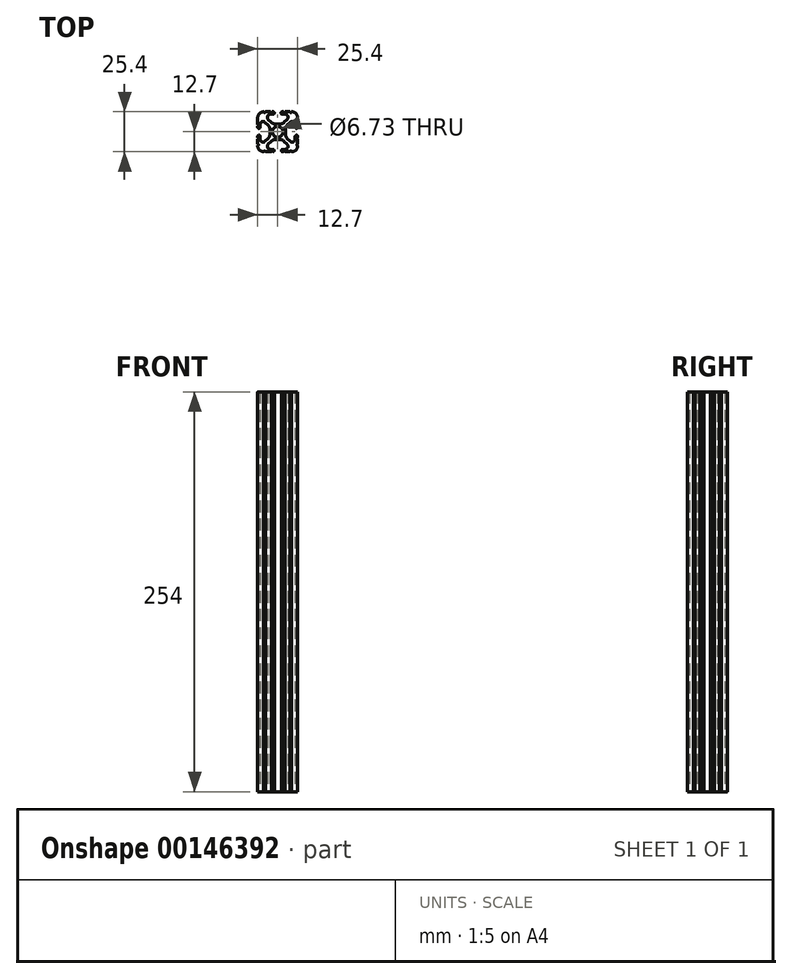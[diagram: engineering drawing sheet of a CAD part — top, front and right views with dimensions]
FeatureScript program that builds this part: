
annotation { "Feature Type Name" : "Feature", "Feature Type Description" : "" }
export const myFeature = defineFeature(function(context is Context, id is Id, definition is map)
    precondition{}
    {
        {
            var Q0;
            Q0=qCreatedBy(makeId("Top.planeOp"),FACE);
            var sketch = newSketch(context, id + "F0", { "sketchPlane" : qUnion([Q0])});
            skCircle(sketch, "E0", {"center": v(-12.7, 12.7) * mm, "radius": 3.36 * mm});
            skLineSegment(sketch, "E1.bottom", {"start": v(-11.24, 17.64) * mm, "end": v(-14.16, 17.64) * mm});
            skLineSegment(sketch, "E1.top", {"start": v(-11.24, 7.76) * mm, "end": v(-14.16, 7.76) * mm});
            skLineSegment(sketch, "E1.left", {"start": v(-7.76, 14.16) * mm, "end": v(-7.76, 11.24) * mm});
            skLineSegment(sketch, "E1.right", {"start": v(-17.64, 14.16) * mm, "end": v(-17.64, 11.24) * mm});
            skPoint(sketch, "E2.visualSharp", {"position": v(-25.4, 25.4) * mm});
            skPoint(sketch, "E3.visualSharp", {"position": v(0, 25.4) * mm});
            skPoint(sketch, "E4.visualSharp", {"position": v(0, 0) * mm});
            skPoint(sketch, "E5.visualSharp", {"position": v(-25.4, 0) * mm});
            skLineSegment(sketch, "E6.0", {"start": v(-18.7, 20.6) * mm, "end": v(-16.85, 18.76) * mm});
            skLineSegment(sketch, "E7.0", {"start": v(-20.6, 18.7) * mm, "end": v(-18.76, 16.85) * mm});
            skPoint(sketch, "E8.orphan", {"position": v(-23.85, 1.55) * mm});
            skPoint(sketch, "E9.orphan", {"position": v(-23.85, 23.85) * mm});
            skPoint(sketch, "E10.orphan", {"position": v(-1.55, 23.85) * mm});
            skPoint(sketch, "E11.orphan", {"position": v(-1.55, 1.55) * mm});
            skLineSegment(sketch, "E12", {"start": v(-8.55, 6.64) * mm, "end": v(-6.7, 4.8) * mm});
            skLineSegment(sketch, "E13.0", {"start": v(-18.7, 4.8) * mm, "end": v(-16.85, 6.64) * mm});
            skLineSegment(sketch, "E14.0", {"start": v(-20.6, 6.7) * mm, "end": v(-18.76, 8.55) * mm});
            skLineSegment(sketch, "E15.0", {"start": v(-8.55, 18.76) * mm, "end": v(-6.7, 20.6) * mm});
            skPoint(sketch, "E16.visualSharp", {"position": v(-23.85, 21.95) * mm});
            skArc(sketch, "E16.filletArc", {"start": v(-20.6, 18.7) * mm, "mid": v(-22.68, 19.1) * mm, "end": v(-23.85, 17.35) * mm});
            skPoint(sketch, "E17.visualSharp", {"position": v(-21.95, 23.85) * mm});
            skArc(sketch, "E17.filletArc", {"start": v(-17.35, 23.85) * mm, "mid": v(-19.1, 22.68) * mm, "end": v(-18.7, 20.6) * mm});
            skPoint(sketch, "E18.visualSharp", {"position": v(-5.34, 23.85) * mm});
            skLineSegment(sketch, "E19", {"start": v(-17.35, 23.85) * mm, "end": v(-15.58, 23.85) * mm});
            skLineSegment(sketch, "E20", {"start": v(-23.85, 17.35) * mm, "end": v(-23.85, 15.62) * mm});
            skLineSegment(sketch, "E21", {"start": v(-8.05, 1.55) * mm, "end": v(-9.78, 1.55) * mm});
            skArc(sketch, "E22.filletArc", {"start": v(-6.7, 20.6) * mm, "mid": v(-6.3, 22.68) * mm, "end": v(-8.05, 23.85) * mm});
            skPoint(sketch, "E23.visualSharp", {"position": v(-1.55, 3.45) * mm});
            skPoint(sketch, "E24.visualSharp", {"position": v(-3.45, 1.55) * mm});
            skArc(sketch, "E24.filletArc", {"start": v(-8.05, 1.55) * mm, "mid": v(-6.3, 2.73) * mm, "end": v(-6.7, 4.8) * mm});
            skArc(sketch, "E25.filletArc", {"start": v(-18.7, 4.8) * mm, "mid": v(-19.1, 2.73) * mm, "end": v(-17.35, 1.55) * mm});
            skArc(sketch, "E26.filletArc", {"start": v(-23.85, 8.05) * mm, "mid": v(-22.68, 6.3) * mm, "end": v(-20.6, 6.7) * mm});
            skLineSegment(sketch, "E27.bottom", {"start": v(-4.9, 0) * mm, "end": v(-8.05, 0) * mm});
            skLineSegment(sketch, "E27.top", {"start": v(-4.92, 25.4) * mm, "end": v(-8.05, 25.4) * mm});
            skLineSegment(sketch, "E27.left", {"start": v(0, 4.9) * mm, "end": v(0, 8.05) * mm});
            skLineSegment(sketch, "E27.right", {"start": v(-25.4, 4.9) * mm, "end": v(-25.4, 8.05) * mm});
            skArc(sketch, "E28.filletArc", {"start": v(-25.4, 3.81) * mm, "mid": v(-24.28, 1.12) * mm, "end": v(-21.59, 0) * mm});
            skArc(sketch, "E29.filletArc", {"start": v(-3.81, 0) * mm, "mid": v(-1.12, 1.12) * mm, "end": v(0, 3.8) * mm});
            skArc(sketch, "E30.filletArc", {"start": v(0, 21.59) * mm, "mid": v(-1.12, 24.28) * mm, "end": v(-3.8, 25.4) * mm});
            skArc(sketch, "E31.filletArc", {"start": v(-21.59, 25.4) * mm, "mid": v(-24.28, 24.28) * mm, "end": v(-25.4, 21.59) * mm});
            skPoint(sketch, "E32.newPointA", {"position": v(-17.64, 7.76) * mm});
            skArc(sketch, "E32.filletArc", {"start": v(-14.16, 7.76) * mm, "mid": v(-15.62, 7.47) * mm, "end": v(-16.85, 6.64) * mm});
            skPoint(sketch, "E33.newPointA", {"position": v(-7.76, 7.76) * mm});
            skArc(sketch, "E33.filletArc", {"start": v(-8.55, 6.64) * mm, "mid": v(-9.78, 7.47) * mm, "end": v(-11.24, 7.76) * mm});
            skArc(sketch, "E34.filletArc", {"start": v(-7.76, 11.24) * mm, "mid": v(-7.47, 9.78) * mm, "end": v(-6.64, 8.55) * mm});
            skArc(sketch, "E35.filletArc", {"start": v(-6.64, 16.85) * mm, "mid": v(-7.47, 15.62) * mm, "end": v(-7.76, 14.16) * mm});
            skPoint(sketch, "E36.newPointB", {"position": v(-7.76, 17.64) * mm});
            skArc(sketch, "E36.filletArc", {"start": v(-11.24, 17.64) * mm, "mid": v(-9.78, 17.93) * mm, "end": v(-8.55, 18.76) * mm});
            skPoint(sketch, "E37.newPointB", {"position": v(-17.64, 17.64) * mm});
            skArc(sketch, "E37.filletArc", {"start": v(-16.85, 18.76) * mm, "mid": v(-15.62, 17.93) * mm, "end": v(-14.16, 17.64) * mm});
            skArc(sketch, "E38.filletArc", {"start": v(-17.64, 14.16) * mm, "mid": v(-17.93, 15.62) * mm, "end": v(-18.76, 16.85) * mm});
            skArc(sketch, "E39.filletArc", {"start": v(-18.76, 8.55) * mm, "mid": v(-17.93, 9.78) * mm, "end": v(-17.64, 11.24) * mm});
            skLineSegment(sketch, "E40", {"start": v(-6.64, 8.55) * mm, "end": v(-4.8, 6.7) * mm});
            skPoint(sketch, "E41.visualSharp", {"position": v(-1.55, 21.95) * mm});
            skArc(sketch, "E42.filletArc", {"start": v(-4.8, 6.7) * mm, "mid": v(-2.73, 6.3) * mm, "end": v(-1.55, 8.05) * mm});
            skLineSegment(sketch, "E43", {"start": v(-1.55, 8.05) * mm, "end": v(-1.55, 9.78) * mm});
            skLineSegment(sketch, "E44", {"start": v(-6.64, 16.85) * mm, "end": v(-4.8, 18.7) * mm});
            skArc(sketch, "E45.filletArc", {"start": v(-1.55, 17.35) * mm, "mid": v(-2.73, 19.1) * mm, "end": v(-4.8, 18.7) * mm});
            skArc(sketch, "E46", {"start": v(-23.85, 9.78) * mm, "mid": v(-24.63, 10.56) * mm, "end": v(-25.4, 9.78) * mm});
            skArc(sketch, "E47", {"start": v(-25.4, 15.62) * mm, "mid": v(-24.63, 14.86) * mm, "end": v(-23.85, 15.62) * mm});
            skArc(sketch, "E48", {"start": v(-15.62, 23.85) * mm, "mid": v(-14.83, 24.63) * mm, "end": v(-15.62, 25.4) * mm});
            skArc(sketch, "E49", {"start": v(-9.78, 25.4) * mm, "mid": v(-10.6, 24.63) * mm, "end": v(-9.78, 23.85) * mm});
            skArc(sketch, "E50", {"start": v(-1.55, 15.62) * mm, "mid": v(-0.77, 14.88) * mm, "end": v(0, 15.62) * mm});
            skArc(sketch, "E51", {"start": v(0, 9.78) * mm, "mid": v(-0.77, 10.5) * mm, "end": v(-1.55, 9.78) * mm});
            skArc(sketch, "E52", {"start": v(-9.78, 1.55) * mm, "mid": v(-10.4, 0.77) * mm, "end": v(-9.78, 0) * mm});
            skArc(sketch, "E53", {"start": v(-15.62, 0) * mm, "mid": v(-14.85, 0.77) * mm, "end": v(-15.62, 1.55) * mm});
            skLineSegment(sketch, "E54.trimOffspring", {"start": v(-15.62, 1.55) * mm, "end": v(-17.35, 1.55) * mm});
            skLineSegment(sketch, "E55.trimOffspring", {"start": v(-16.7, 0) * mm, "end": v(-20.5, 0) * mm});
            skLineSegment(sketch, "E56.trimOffspring", {"start": v(-1.55, 15.62) * mm, "end": v(-1.55, 17.35) * mm});
            skLineSegment(sketch, "E57.trimOffspring", {"start": v(0, 15.62) * mm, "end": v(0, 16.26) * mm});
            skLineSegment(sketch, "E58.trimOffspring", {"start": v(-23.85, 9.78) * mm, "end": v(-23.85, 8.05) * mm});
            skLineSegment(sketch, "E59.trimOffspring", {"start": v(-25.4, 15.62) * mm, "end": v(-25.4, 16.26) * mm});
            skLineSegment(sketch, "E60.trimOffspring", {"start": v(-9.86, 23.85) * mm, "end": v(-8.05, 23.85) * mm});
            skLineSegment(sketch, "E61.trimOffspring", {"start": v(-15.58, 25.4) * mm, "end": v(-16.25, 25.4) * mm});
            skPoint(sketch, "E62.start.orphan", {"position": v(-15.62, 17.93) * mm});
            skPoint(sketch, "E63.start.orphan", {"position": v(-9.78, 17.93) * mm});
            skPoint(sketch, "E64.start.orphan", {"position": v(-7.47, 15.62) * mm});
            skPoint(sketch, "E65.start.orphan", {"position": v(-7.47, 9.78) * mm});
            skPoint(sketch, "E66.start.orphan", {"position": v(-17.93, 15.62) * mm});
            skPoint(sketch, "E67.start.orphan", {"position": v(-17.93, 9.78) * mm});
            skPoint(sketch, "E68.start.orphan", {"position": v(-9.78, 7.47) * mm});
            skPoint(sketch, "E69.start.orphan", {"position": v(-15.62, 7.47) * mm});
            skPoint(sketch, "E70.endSnap0", {"position": v(0, 18.6) * mm});
            skPoint(sketch, "E71.startSnap0", {"position": v(-1.55, 8.92) * mm});
            skArc(sketch, "E72", {"start": v(-4.92, 25.4) * mm, "mid": v(-4.37, 24.9) * mm, "end": v(-3.81, 25.4) * mm});
            skArc(sketch, "E73", {"start": v(-9.14, 25.4) * mm, "mid": v(-8.6, 24.86) * mm, "end": v(-8.05, 25.4) * mm});
            skArc(sketch, "E74", {"start": v(-17.35, 25.4) * mm, "mid": v(-16.8, 24.86) * mm, "end": v(-16.25, 25.4) * mm});
            skArc(sketch, "E75", {"start": v(-21.59, 25.4) * mm, "mid": v(-21.04, 24.85) * mm, "end": v(-20.49, 25.4) * mm});
            skLineSegment(sketch, "E76", {"start": v(-25.4, 21.59) * mm, "end": v(-25.4, 20.5) * mm});
            skArc(sketch, "E77", {"start": v(-25.4, 16.26) * mm, "mid": v(-24.84, 16.8) * mm, "end": v(-25.4, 17.35) * mm});
            skArc(sketch, "E78", {"start": v(-25.4, 8.05) * mm, "mid": v(-24.9, 8.6) * mm, "end": v(-25.4, 9.15) * mm});
            skArc(sketch, "E79", {"start": v(-25.4, 3.81) * mm, "mid": v(-24.85, 4.36) * mm, "end": v(-25.4, 4.9) * mm});
            skArc(sketch, "E80", {"start": v(-20.5, 0) * mm, "mid": v(-21.04, 0.55) * mm, "end": v(-21.59, 0) * mm});
            skArc(sketch, "E81", {"start": v(-15.62, 0) * mm, "mid": v(-16.16, 0.54) * mm, "end": v(-16.7, 0) * mm});
            skArc(sketch, "E82", {"start": v(-8.05, 0) * mm, "mid": v(-8.6, 0.55) * mm, "end": v(-9.15, 0) * mm});
            skArc(sketch, "E83", {"start": v(-3.81, 0) * mm, "mid": v(-4.35, 0.54) * mm, "end": v(-4.9, 0) * mm});
            skLineSegment(sketch, "E84.trimOffspring", {"start": v(-17.35, 25.4) * mm, "end": v(-20.49, 25.4) * mm});
            skLineSegment(sketch, "E85.trimOffspring", {"start": v(-25.4, 17.35) * mm, "end": v(-25.4, 21.59) * mm});
            skLineSegment(sketch, "E86.trimOffspring", {"start": v(-25.4, 9.15) * mm, "end": v(-25.4, 9.78) * mm});
            skLineSegment(sketch, "E87.trimOffspring", {"start": v(-9.15, 0) * mm, "end": v(-9.78, 0) * mm});
            skArc(sketch, "E88", {"start": v(0, 4.9) * mm, "mid": v(-0.54, 4.36) * mm, "end": v(0, 3.8) * mm});
            skArc(sketch, "E89", {"start": v(0, 9.15) * mm, "mid": v(-0.54, 8.6) * mm, "end": v(0, 8.05) * mm});
            skLineSegment(sketch, "E90.trimOffspring", {"start": v(0, 9.15) * mm, "end": v(0, 9.78) * mm});
            skArc(sketch, "E91", {"start": v(0, 21.59) * mm, "mid": v(-0.55, 21.04) * mm, "end": v(0, 20.5) * mm});
            skArc(sketch, "E92", {"start": v(0, 17.35) * mm, "mid": v(-0.55, 16.8) * mm, "end": v(0, 16.26) * mm});
            skLineSegment(sketch, "E93.trimOffspring", {"start": v(0, 17.35) * mm, "end": v(0, 20.5) * mm});
            skLineSegment(sketch, "E94.trimOffspring", {"start": v(-9.14, 25.4) * mm, "end": v(-9.86, 25.4) * mm});
            skSolve(sketch);
        }
        {
            var Q0;
            Q0=qSketchRegion(id+"F0",true);
            extrude(context, id + "F1", {"entities" : qUnion([Q0]), "depth" : 254 * mm});
        }
    });
